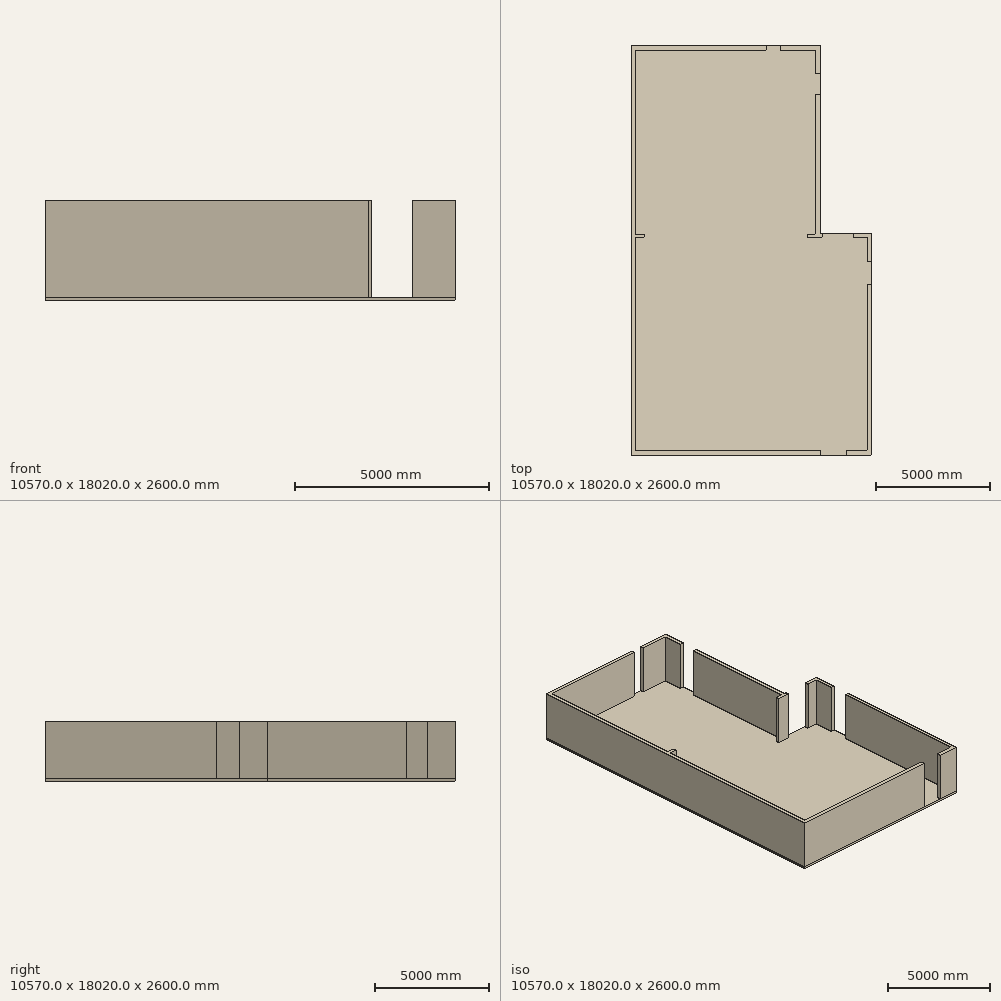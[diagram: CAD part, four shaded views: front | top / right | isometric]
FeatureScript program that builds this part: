
annotation { "Feature Type Name" : "Feature", "Feature Type Description" : "" }
export const myFeature = defineFeature(function(context is Context, id is Id, definition is map)
    precondition{}
    {
        {
            var Q0;
            Q0=qCreatedBy(makeId("Top.planeOp"),FACE);
            var sketch = newSketch(context, id + "F0", { "sketchPlane" : qUnion([Q0])});
            skLineSegment(sketch, "E0", {"start": v(0, 0) * mm, "end": v(8120, 0) * mm});
            skLineSegment(sketch, "E1", {"start": v(9250, 0) * mm, "end": v(10170, 0) * mm});
            skLineSegment(sketch, "E2", {"start": v(10170, 0) * mm, "end": v(10170, 7310) * mm});
            skLineSegment(sketch, "E3", {"start": v(10170, 8310) * mm, "end": v(10170, 9360) * mm});
            skLineSegment(sketch, "E4", {"start": v(10170, 9360) * mm, "end": v(9590, 9360) * mm});
            skLineSegment(sketch, "E5", {"start": v(8210, 9360) * mm, "end": v(7550, 9360) * mm});
            skLineSegment(sketch, "E6", {"start": v(7550, 9360) * mm, "end": v(7550, 9530) * mm});
            skLineSegment(sketch, "E7", {"start": v(7550, 9530) * mm, "end": v(7910, 9530) * mm});
            skLineSegment(sketch, "E8", {"start": v(7910, 9530) * mm, "end": v(7910, 15680) * mm});
            skLineSegment(sketch, "E9", {"start": v(7910, 16580) * mm, "end": v(7910, 17620) * mm});
            skLineSegment(sketch, "E10", {"start": v(7910, 17620) * mm, "end": v(6380, 17620) * mm});
            skLineSegment(sketch, "E11", {"start": v(5750, 17620) * mm, "end": v(0, 17620) * mm});
            skLineSegment(sketch, "E12", {"start": v(0, 17620) * mm, "end": v(0, 9530) * mm});
            skLineSegment(sketch, "E13", {"start": v(0, 9530) * mm, "end": v(380, 9530) * mm});
            skLineSegment(sketch, "E14", {"start": v(380, 9530) * mm, "end": v(380, 9360) * mm});
            skLineSegment(sketch, "E15", {"start": v(380, 9360) * mm, "end": v(0, 9360) * mm});
            skLineSegment(sketch, "E16", {"start": v(0, 9360) * mm, "end": v(0, 0) * mm});
            skLineSegment(sketch, "E17", {"start": v(-200, 17820) * mm, "end": v(-200, -200) * mm});
            skLineSegment(sketch, "E18", {"start": v(8120, -200) * mm, "end": v(8120, 0) * mm});
            skLineSegment(sketch, "E19", {"start": v(-200, -200) * mm, "end": v(8120, -200) * mm});
            skLineSegment(sketch, "E20", {"start": v(-200, 17820) * mm, "end": v(5750, 17820) * mm});
            skLineSegment(sketch, "E21", {"start": v(5750, 17820) * mm, "end": v(5750, 17620) * mm});
            skLineSegment(sketch, "E22", {"start": v(6380, 17620) * mm, "end": v(6380, 17820) * mm});
            skLineSegment(sketch, "E23", {"start": v(6380, 17820) * mm, "end": v(8110, 17820) * mm});
            skLineSegment(sketch, "E24", {"start": v(8110, 17820) * mm, "end": v(8110, 16580) * mm});
            skLineSegment(sketch, "E25", {"start": v(8110, 16580) * mm, "end": v(7910, 16580) * mm});
            skLineSegment(sketch, "E26", {"start": v(7910, 15680) * mm, "end": v(8110, 15680) * mm});
            skLineSegment(sketch, "E27", {"start": v(8110, 15680) * mm, "end": v(8110, 9560) * mm});
            skLineSegment(sketch, "E28", {"start": v(8110, 9560) * mm, "end": v(8210, 9560) * mm});
            skLineSegment(sketch, "E29", {"start": v(8210, 9560) * mm, "end": v(8210, 9360) * mm});
            skLineSegment(sketch, "E30", {"start": v(9590, 9360) * mm, "end": v(9590, 9560) * mm});
            skLineSegment(sketch, "E31", {"start": v(9590, 9560) * mm, "end": v(10370, 9560) * mm});
            skLineSegment(sketch, "E32", {"start": v(10370, 9560) * mm, "end": v(10370, 8310) * mm});
            skLineSegment(sketch, "E33", {"start": v(10370, 8310) * mm, "end": v(10170, 8310) * mm});
            skLineSegment(sketch, "E34", {"start": v(10170, 7310) * mm, "end": v(10370, 7310) * mm});
            skLineSegment(sketch, "E35", {"start": v(10370, 7310) * mm, "end": v(10370, -200) * mm});
            skLineSegment(sketch, "E36", {"start": v(10370, -200) * mm, "end": v(9250, -200) * mm});
            skLineSegment(sketch, "E37", {"start": v(9250, -200) * mm, "end": v(9250, 0) * mm});
            skSolve(sketch);
        }
        {
            var Q0;
            Q0=makeQuery(id+"F0.imprint","IMPRINT",FACE,{"disambiguationData":[TD([[makeQuery(id+"F0.imprint","IMPRINT",EDGE,{"derivedFrom":sQuery(id+"F0.wireOp",EDGE,"E0")}),-1.0]])]});
            var Q1;
            Q1=makeQuery(id+"F0.imprint","IMPRINT",FACE,{"disambiguationData":[TD([[makeQuery(id+"F0.imprint","IMPRINT",EDGE,{"derivedFrom":sQuery(id+"F0.wireOp",EDGE,"E9")}),-1.0]])]});
            var Q2;
            Q2=makeQuery(id+"F0.imprint","IMPRINT",FACE,{"disambiguationData":[TD([[makeQuery(id+"F0.imprint","IMPRINT",EDGE,{"derivedFrom":sQuery(id+"F0.wireOp",EDGE,"E5")}),-1.0]])]});
            var Q3;
            Q3=makeQuery(id+"F0.imprint","IMPRINT",FACE,{"disambiguationData":[TD([[makeQuery(id+"F0.imprint","IMPRINT",EDGE,{"derivedFrom":sQuery(id+"F0.wireOp",EDGE,"E3")}),-1.0]])]});
            var Q4;
            Q4=makeQuery(id+"F0.imprint","IMPRINT",FACE,{"disambiguationData":[TD([[makeQuery(id+"F0.imprint","IMPRINT",EDGE,{"derivedFrom":sQuery(id+"F0.wireOp",EDGE,"E1")}),-1.0]])]});
            extrude(context, id + "F1", {"entities" : qUnion([Q0, Q1, Q2, Q3, Q4]), "depth" : 2500 * mm});
        }
        {
            var Q0;
            Q0=makeQuery(id+"F1.opExtrude","CAP_FACE",FACE,{"disambiguationData":[OSD([sQuery(id+"F0.wireOp",EDGE,"E0"),sQuery(id+"F0.wireOp",EDGE,"E11"),sQuery(id+"F0.wireOp",EDGE,"E12"),sQuery(id+"F0.wireOp",EDGE,"E13"),sQuery(id+"F0.wireOp",EDGE,"E14"),sQuery(id+"F0.wireOp",EDGE,"E15"),sQuery(id+"F0.wireOp",EDGE,"E16"),sQuery(id+"F0.wireOp",EDGE,"E17"),sQuery(id+"F0.wireOp",EDGE,"E18"),sQuery(id+"F0.wireOp",EDGE,"E19"),sQuery(id+"F0.wireOp",EDGE,"E20"),sQuery(id+"F0.wireOp",EDGE,"E21")])],"isStart":true});
            var sketch = newSketch(context, id + "F2", { "sketchPlane" : qUnion([Q0])});
            skLineSegment(sketch, "E38", {"start": v(-200, 200) * mm, "end": v(10370, 200) * mm});
            skLineSegment(sketch, "E39", {"start": v(10370, 200) * mm, "end": v(10370, -9560) * mm});
            skLineSegment(sketch, "E40", {"start": v(10370, -9560) * mm, "end": v(8110, -9560) * mm});
            skLineSegment(sketch, "E41", {"start": v(8110, -9560) * mm, "end": v(8110, -17820) * mm});
            skLineSegment(sketch, "E42", {"start": v(8110, -17820) * mm, "end": v(-200, -17820) * mm});
            skLineSegment(sketch, "E43", {"start": v(-200, -17820) * mm, "end": v(-200, 200) * mm});
            skSolve(sketch);
        }
        {
            var Q0;
            Q0 = qSketchRegion(id + "F2", true);
            extrude(context, id + "F3", {"entities" : qUnion([Q0]), "depth" : 100 * mm});
        }
    });
